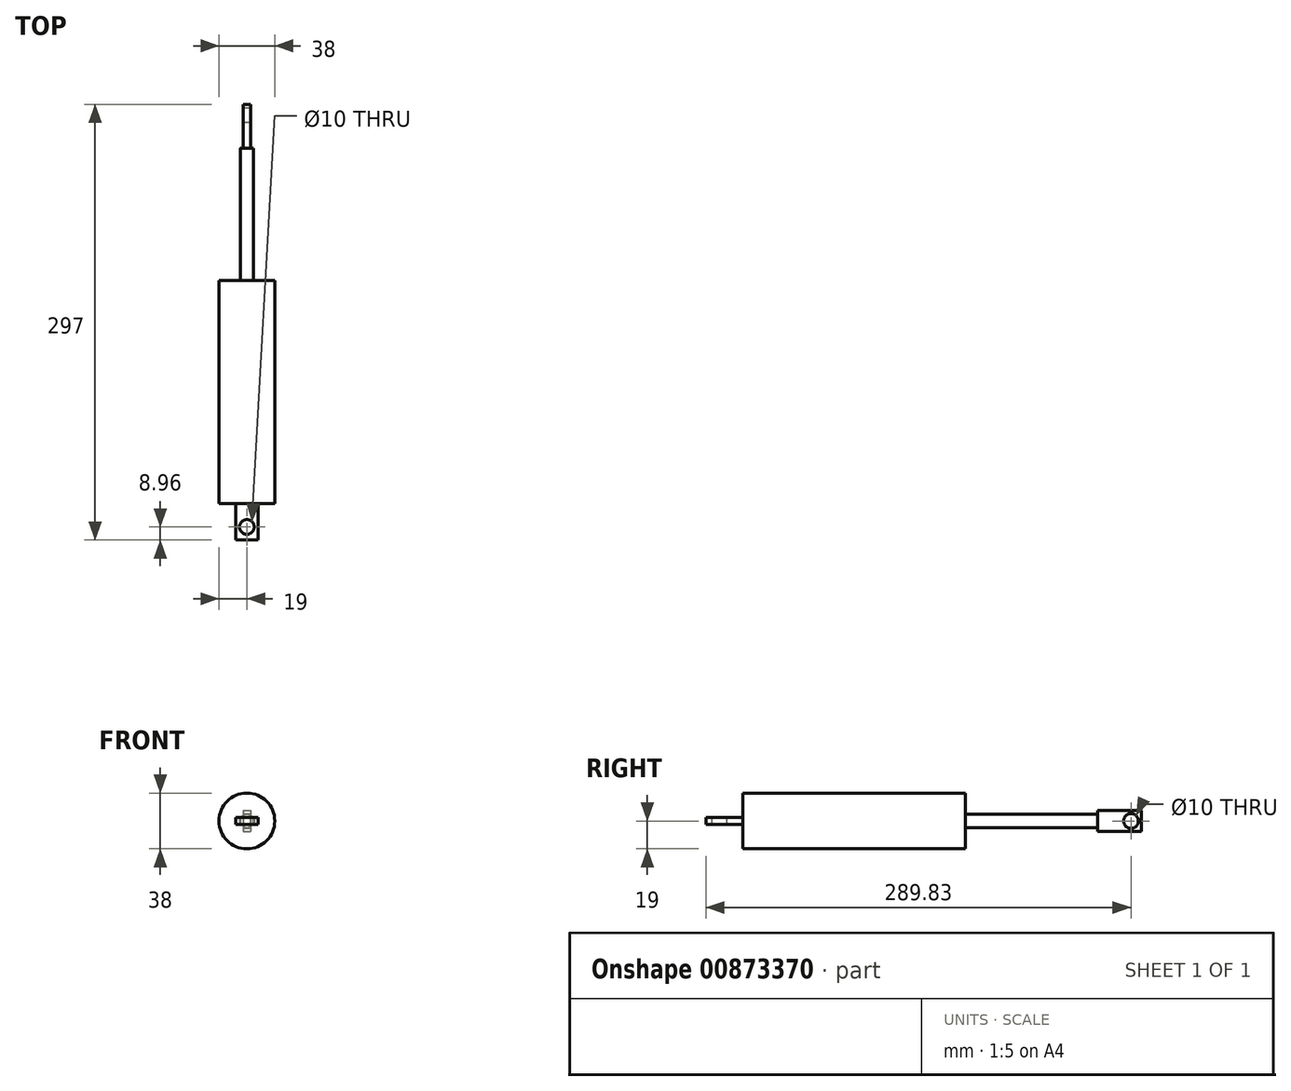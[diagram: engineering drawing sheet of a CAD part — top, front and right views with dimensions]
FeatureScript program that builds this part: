
annotation { "Feature Type Name" : "Feature", "Feature Type Description" : "" }
export const myFeature = defineFeature(function(context is Context, id is Id, definition is map)
    precondition{}
    {
        {
            var Q0;
            Q0=qCreatedBy(makeId("Front.planeOp"),FACE);
            var sketch = newSketch(context, id + "F0", { "sketchPlane" : qUnion([Q0])});
            skCircle(sketch, "E0", {"center": v(0, 0) * mm, "radius": 19 * mm});
            skSolve(sketch);
        }
        {
            var Q0;
            Q0=makeQuery(id+"F0.imprint","IMPRINT",FACE,{"disambiguationData":[TD([[makeQuery(id+"F0.imprint","IMPRINT",EDGE,{"derivedFrom":sQuery(id+"F0.wireOp",EDGE,"E0")}),1.0]])]});
            extrude(context, id + "F1", {"entities" : qUnion([Q0]), "depth" : 152 * mm, "offsetDistance" : 25 * mm});
        }
        {
            var Q0;
            Q0=makeQuery(id+"F1.opExtrude","CAP_FACE",FACE,{"disambiguationData":[OSD([sQuery(id+"F0.wireOp",EDGE,"E0")])],"isStart":true});
            var sketch = newSketch(context, id + "F2", { "sketchPlane" : qUnion([Q0])});
            skCircle(sketch, "E1", {"center": v(0, 0) * mm, "radius": 4.5 * mm});
            skSolve(sketch);
        }
        {
            var Q0;
            Q0=makeQuery(id+"F2.imprint","IMPRINT",FACE,{"disambiguationData":[TD([[makeQuery(id+"F2.imprint","IMPRINT",EDGE,{"derivedFrom":sQuery(id+"F2.wireOp",EDGE,"E1")}),1.0]])]});
            extrude(context, id + "F3", {"entities" : qUnion([Q0]), "depth" : 90 * mm, "offsetDistance" : 25 * mm});
        }
        {
            var Q0;
            Q0=makeQuery(id+"F3.opExtrude","CAP_FACE",FACE,{"disambiguationData":[OSD([sQuery(id+"F2.wireOp",EDGE,"E1")])],"isStart":false});
            var sketch = newSketch(context, id + "F4", { "sketchPlane" : qUnion([Q0])});
            skLineSegment(sketch, "E2.bottom", {"start": v(2.5, 7) * mm, "end": v(-2.5, 7) * mm});
            skLineSegment(sketch, "E2.top", {"start": v(2.5, -7) * mm, "end": v(-2.5, -7) * mm});
            skLineSegment(sketch, "E2.left", {"start": v(2.5, 7) * mm, "end": v(2.5, -7) * mm});
            skLineSegment(sketch, "E2.right", {"start": v(-2.5, 7) * mm, "end": v(-2.5, -7) * mm});
            skPoint(sketch, "E2.middle", {"position": v(0, 0) * mm});
            skSolve(sketch);
        }
        {
            var Q0;
            {var subQ0=sQuery(id+"F4.wireOp",EDGE,"E2.top");Q0=makeQuery(id+"F4.imprint","IMPRINT",FACE,{"disambiguationData":[TD([[makeQuery(id+"F4.imprint","IMPRINT",EDGE,{"derivedFrom":subQ0}),-1.0]])]});}
            var Q1;
            {var subQ0=sQuery(id+"F4.wireOp",EDGE,"E2.left");var subQ1=makeQuery(id+"F3.opExtrude","CAP_EDGE",EDGE,{"disambiguationData":[OSD([sQuery(id+"F2.wireOp",EDGE,"E1")])],"isStart":false});var subQ2=makeQuery(id+"F4.imprint","INTERSECT",VERTEX,{"disambiguationData":[OD(0.0)],"derivedFrom":[subQ1,subQ0]});Q1=makeQuery(id+"F4.imprint","IMPRINT",FACE,{"disambiguationData":[TD([[makeQuery(id+"F4.imprint","IMPRINT",EDGE,{"disambiguationData":[TD([[subQ2,-1.0]])],"derivedFrom":subQ0}),-1.0]])]});}
            var Q2;
            {var subQ0=sQuery(id+"F4.wireOp",EDGE,"E2.bottom");Q2=makeQuery(id+"F4.imprint","IMPRINT",FACE,{"disambiguationData":[TD([[makeQuery(id+"F4.imprint","IMPRINT",EDGE,{"derivedFrom":subQ0}),1.0]])]});}
            extrude(context, id + "F5", {"entities" : qUnion([Q0, Q1, Q2]), "operationType" : NewBodyOperationType.ADD, "depth" : 30 * mm, "offsetDistance" : 25 * mm});
        }
        {
            var Q0;
            Q0=makeQuery(id+"F5.opExtrude","SWEPT_FACE",FACE,{"disambiguationData":[OSD([sQuery(id+"F4.wireOp",EDGE,"E2.right")])]});
            var sketch = newSketch(context, id + "F6", { "sketchPlane" : qUnion([Q0])});
            skCircle(sketch, "E3", {"center": v(112.83, 0) * mm, "radius": 5 * mm});
            skSolve(sketch);
        }
        {
            var Q0;
            Q0=makeQuery(id+"F6.imprint","IMPRINT",FACE,{"disambiguationData":[TD([[makeQuery(id+"F6.imprint","IMPRINT",EDGE,{"derivedFrom":sQuery(id+"F6.wireOp",EDGE,"E3")}),1.0]])]});
            extrude(context, id + "F7", {"entities" : qUnion([Q0]), "operationType" : NewBodyOperationType.REMOVE, "oppositeDirection" : true, "depth" : 25 * mm, "offsetDistance" : 25 * mm});
        }
        {
            var Q0;
            Q0=makeQuery(id+"F1.opExtrude","CAP_FACE",FACE,{"disambiguationData":[OSD([sQuery(id+"F0.wireOp",EDGE,"E0")])],"isStart":false});
            var sketch = newSketch(context, id + "F8", { "sketchPlane" : qUnion([Q0])});
            skLineSegment(sketch, "E4.bottom", {"start": v(-7.5, 2.5) * mm, "end": v(7.5, 2.5) * mm});
            skLineSegment(sketch, "E4.top", {"start": v(-7.5, -2.5) * mm, "end": v(7.5, -2.5) * mm});
            skLineSegment(sketch, "E4.left", {"start": v(-7.5, 2.5) * mm, "end": v(-7.5, -2.5) * mm});
            skLineSegment(sketch, "E4.right", {"start": v(7.5, 2.5) * mm, "end": v(7.5, -2.5) * mm});
            skPoint(sketch, "E4.middle", {"position": v(0, 0) * mm});
            skSolve(sketch);
        }
        {
            var Q0;
            Q0=makeQuery(id+"F8.imprint","IMPRINT",FACE,{"disambiguationData":[TD([[makeQuery(id+"F8.imprint","IMPRINT",EDGE,{"derivedFrom":sQuery(id+"F8.wireOp",EDGE,"E4.bottom")}),-1.0]])]});
            extrude(context, id + "F9", {"entities" : qUnion([Q0]), "operationType" : NewBodyOperationType.ADD, "depth" : 25 * mm, "offsetDistance" : 25 * mm});
        }
        {
            var Q0;
            Q0=makeQuery(id+"F9.opExtrude","SWEPT_FACE",FACE,{"disambiguationData":[OSD([sQuery(id+"F8.wireOp",EDGE,"E4.top")])]});
            var sketch = newSketch(context, id + "F10", { "sketchPlane" : qUnion([Q0])});
            skCircle(sketch, "E5", {"center": v(0, 168.04) * mm, "radius": 5 * mm});
            skSolve(sketch);
        }
        {
            var Q0;
            Q0=makeQuery(id+"F10.imprint","IMPRINT",FACE,{"disambiguationData":[TD([[makeQuery(id+"F10.imprint","IMPRINT",EDGE,{"derivedFrom":sQuery(id+"F10.wireOp",EDGE,"E5")}),1.0]])]});
            extrude(context, id + "F11", {"entities" : qUnion([Q0]), "operationType" : NewBodyOperationType.REMOVE, "oppositeDirection" : true, "depth" : 25 * mm, "offsetDistance" : 25 * mm});
        }
    });
